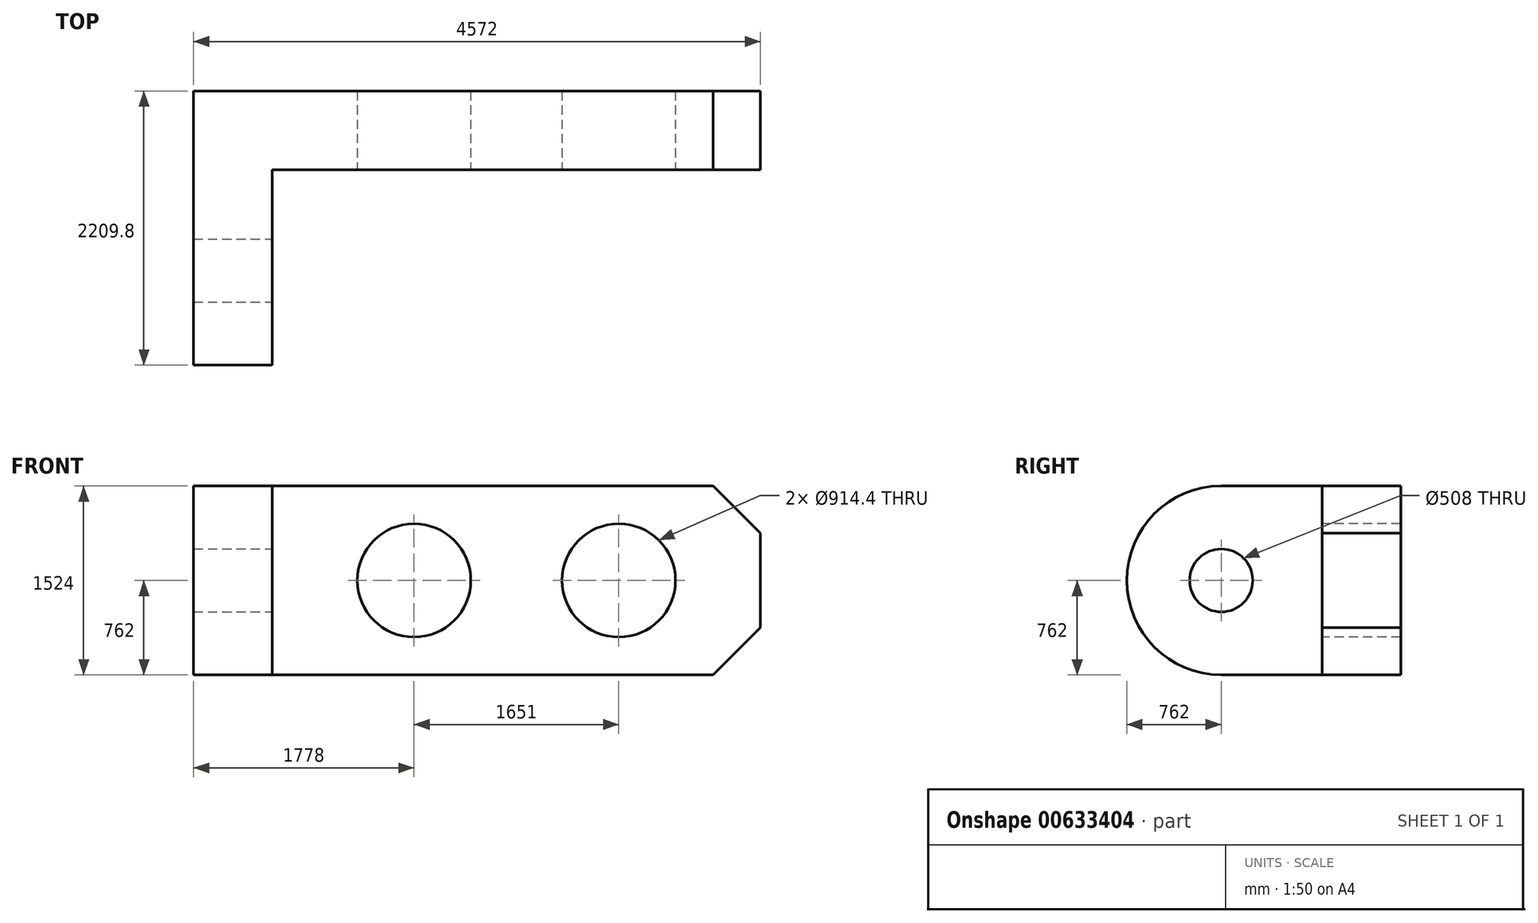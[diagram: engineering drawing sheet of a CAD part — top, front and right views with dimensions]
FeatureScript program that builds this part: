
annotation { "Feature Type Name" : "Feature", "Feature Type Description" : "" }
export const myFeature = defineFeature(function(context is Context, id is Id, definition is map)
    precondition{}
    {
        {
            var Q0;
            Q0=qCreatedBy(makeId("Front.planeOp"),FACE);
            var sketch = newSketch(context, id + "F0", { "sketchPlane" : qUnion([Q0])});
            skLineSegment(sketch, "E0.bottom", {"start": v(-2286, 762) * mm, "end": v(2286, 762) * mm});
            skLineSegment(sketch, "E0.top", {"start": v(-2286, -762) * mm, "end": v(2286, -762) * mm});
            skLineSegment(sketch, "E0.left", {"start": v(-2286, 762) * mm, "end": v(-2286, -762) * mm});
            skLineSegment(sketch, "E0.right", {"start": v(2286, 762) * mm, "end": v(2286, -762) * mm});
            skPoint(sketch, "E0.middle", {"position": v(0, 0) * mm});
            skSolve(sketch);
        }
        {
            var Q0;
            Q0=makeQuery(id+"F0.imprint","IMPRINT",FACE,{"disambiguationData":[TD([[makeQuery(id+"F0.imprint","IMPRINT",EDGE,{"derivedFrom":sQuery(id+"F0.wireOp",EDGE,"E0.bottom")}),-1.0]])]});
            extrude(context, id + "F1", {"entities" : qUnion([Q0]), "depth" : 635 * mm, "offsetDistance" : 25.4 * mm});
        }
        {
            var Q0;
            Q0=makeQuery(id+"F1.opExtrude","CAP_FACE",FACE,{"disambiguationData":[OSD([sQuery(id+"F0.wireOp",EDGE,"E0.bottom"),sQuery(id+"F0.wireOp",EDGE,"E0.top"),sQuery(id+"F0.wireOp",EDGE,"E0.left"),sQuery(id+"F0.wireOp",EDGE,"E0.right")])],"isStart":false});
            var sketch = newSketch(context, id + "F2", { "sketchPlane" : qUnion([Q0])});
            skLineSegment(sketch, "E1.bottom", {"start": v(-2286, 762) * mm, "end": v(-1651, 762) * mm});
            skLineSegment(sketch, "E1.top", {"start": v(-2286, -762) * mm, "end": v(-1651, -762) * mm});
            skLineSegment(sketch, "E1.left", {"start": v(-2286, 762) * mm, "end": v(-2286, -762) * mm});
            skLineSegment(sketch, "E1.right", {"start": v(-1651, 762) * mm, "end": v(-1651, -762) * mm});
            skSolve(sketch);
        }
        {
            var Q0;
            Q0=makeQuery(id+"F2.imprint","IMPRINT",FACE,{"disambiguationData":[TD([[makeQuery(id+"F2.imprint","IMPRINT",EDGE,{"derivedFrom":sQuery(id+"F2.wireOp",EDGE,"E1.bottom")}),-1.0]])]});
            extrude(context, id + "F3", {"entities" : qUnion([Q0]), "operationType" : NewBodyOperationType.ADD, "depth" : 1574.8 * mm, "offsetDistance" : 25.4 * mm});
        }
        {
            var Q0;
            Q0=makeQuery(id+"F3.opExtrude","CAP_EDGE",EDGE,{"disambiguationData":[OSD([sQuery(id+"F2.wireOp",EDGE,"E1.bottom")])],"isStart":false});
            var Q1;
            Q1=makeQuery(id+"F3.opExtrude","CAP_EDGE",EDGE,{"disambiguationData":[OSD([sQuery(id+"F2.wireOp",EDGE,"E1.top")])],"isStart":false});
            fillet(context, id + "F4", {"entities" : qUnion([Q0, Q1]), "radius" : 762 * mm, "tangentPropagation" : true, "allowEdgeOverflow" : false});
        }
        {
            var Q0;
            Q0=makeQuery(id+"F1.opExtrude","CAP_FACE",FACE,{"disambiguationData":[OSD([sQuery(id+"F0.wireOp",EDGE,"E0.bottom"),sQuery(id+"F0.wireOp",EDGE,"E0.top"),sQuery(id+"F0.wireOp",EDGE,"E0.left"),sQuery(id+"F0.wireOp",EDGE,"E0.right")])],"isStart":false});
            var sketch = newSketch(context, id + "F5", { "sketchPlane" : qUnion([Q0])});
            skCircle(sketch, "E2", {"center": v(-508, 0) * mm, "radius": 457.2 * mm});
            skCircle(sketch, "E3", {"center": v(1143, 0) * mm, "radius": 457.2 * mm});
            skSolve(sketch);
        }
        {
            var Q0;
            Q0=makeQuery(id+"F5.imprint","IMPRINT",FACE,{"disambiguationData":[TD([[makeQuery(id+"F5.imprint","IMPRINT",EDGE,{"derivedFrom":sQuery(id+"F5.wireOp",EDGE,"E2")}),1.0]])]});
            var Q1;
            Q1=makeQuery(id+"F5.imprint","IMPRINT",FACE,{"disambiguationData":[TD([[makeQuery(id+"F5.imprint","IMPRINT",EDGE,{"derivedFrom":sQuery(id+"F5.wireOp",EDGE,"E3")}),1.0]])]});
            var Q2;
            Q2=sQuery(id+"F5.wireOp",EDGE,"E2");
            var Q3;
            Q3=sQuery(id+"F5.wireOp",EDGE,"E3");
            extrude(context, id + "F6", {"entities" : qUnion([Q0, Q1]), "operationType" : NewBodyOperationType.REMOVE, "surfaceEntities" : qUnion([Q2, Q3]), "oppositeDirection" : true, "depth" : 635 * mm, "offsetDistance" : 25.4 * mm});
        }
        {
            var Q0;
            Q0=makeQuery(id+"F3.opExtrude","SWEPT_FACE",FACE,{"disambiguationData":[OSD([sQuery(id+"F2.wireOp",EDGE,"E1.right")])]});
            var sketch = newSketch(context, id + "F7", { "sketchPlane" : qUnion([Q0])});
            skCircle(sketch, "E4", {"center": v(-1447.8, 0) * mm, "radius": 254 * mm});
            skSolve(sketch);
        }
        {
            var Q0;
            Q0=makeQuery(id+"F7.imprint","IMPRINT",FACE,{"disambiguationData":[TD([[makeQuery(id+"F7.imprint","IMPRINT",EDGE,{"derivedFrom":sQuery(id+"F7.wireOp",EDGE,"E4")}),1.0]])]});
            extrude(context, id + "F8", {"entities" : qUnion([Q0]), "operationType" : NewBodyOperationType.REMOVE, "endBound" : BoundingType.THROUGH_ALL, "oppositeDirection" : true, "depth" : 25.4 * mm, "offsetDistance" : 25.4 * mm});
        }
        {
            var Q0;
            Q0=makeQuery(id+"F1.opExtrude","SWEPT_EDGE",EDGE,{"disambiguationData":[OSD([sQuery(id+"F0.wireOp",EDGE,"E0.top"),sQuery(id+"F0.wireOp",EDGE,"E0.right")])]});
            var Q1;
            Q1=makeQuery(id+"F1.opExtrude","SWEPT_EDGE",EDGE,{"disambiguationData":[OSD([sQuery(id+"F0.wireOp",EDGE,"E0.bottom"),sQuery(id+"F0.wireOp",EDGE,"E0.right")])]});
            chamfer(context, id + "F9", {"entities" : qUnion([Q0, Q1]), "width" : 381 * mm, "tangentPropagation" : true});
        }
    });
